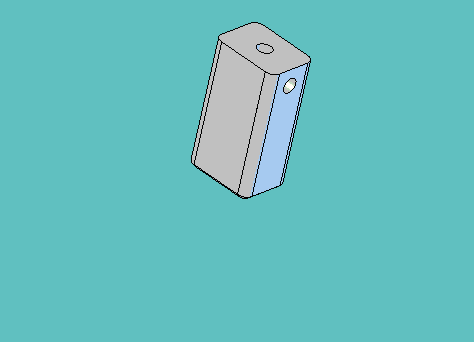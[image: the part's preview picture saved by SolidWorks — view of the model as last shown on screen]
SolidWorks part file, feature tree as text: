
SOLIDWORKS PART (.sldprt)
format: sldprt  version: not decoded by parser v0  size: 384,000 bytes
history: native  units: mm
features: sketch x4, cut_extrude x2, material x1, revolve x1, extrude x1, fillet x1, chamfer x1 (+11 scaffold rows collapsed)
feature tree (22):
  scaffold x11  (default folders/planes/origin — collapsed)
  material  "Material <not specified>"
  sketch  "Sketch1"  dims[D1=~23.41245mm D2=9.525mm D3=6.0452mm D4=~45.24375mm]
  revolve  "Revolve1"  Angle=360deg
  sketch  "Sketch5"  dims[D3=12.7mm D1=4.7625mm D2=4.7625mm]
  extrude  "Extrude1"  [1 undecoded]
  sketch  "Sketch3"  dims[D1=2.7051mm]
  cut_extrude  "Cut-Extrude2"  [1 undecoded]
  sketch  "Sketch4"  dims[D2=2.7051mm D1=3.175mm]
  cut_extrude  "Cut-Extrude3"  [1 undecoded]
  fillet  "Fillet1"  Radius=1.5875mm
  chamfer  "Chamfer1"  Distance=0.762mm Angle=45deg
decode coverage: 7 of 10 modeling features carry decoded parameters
note: ~ marks probable driven/reference dimensions
note: 3 parameter values undecoded
summary: no parameter record found for 3 features
note: suppression state not decoded; provenance and decode notes live in map.json
